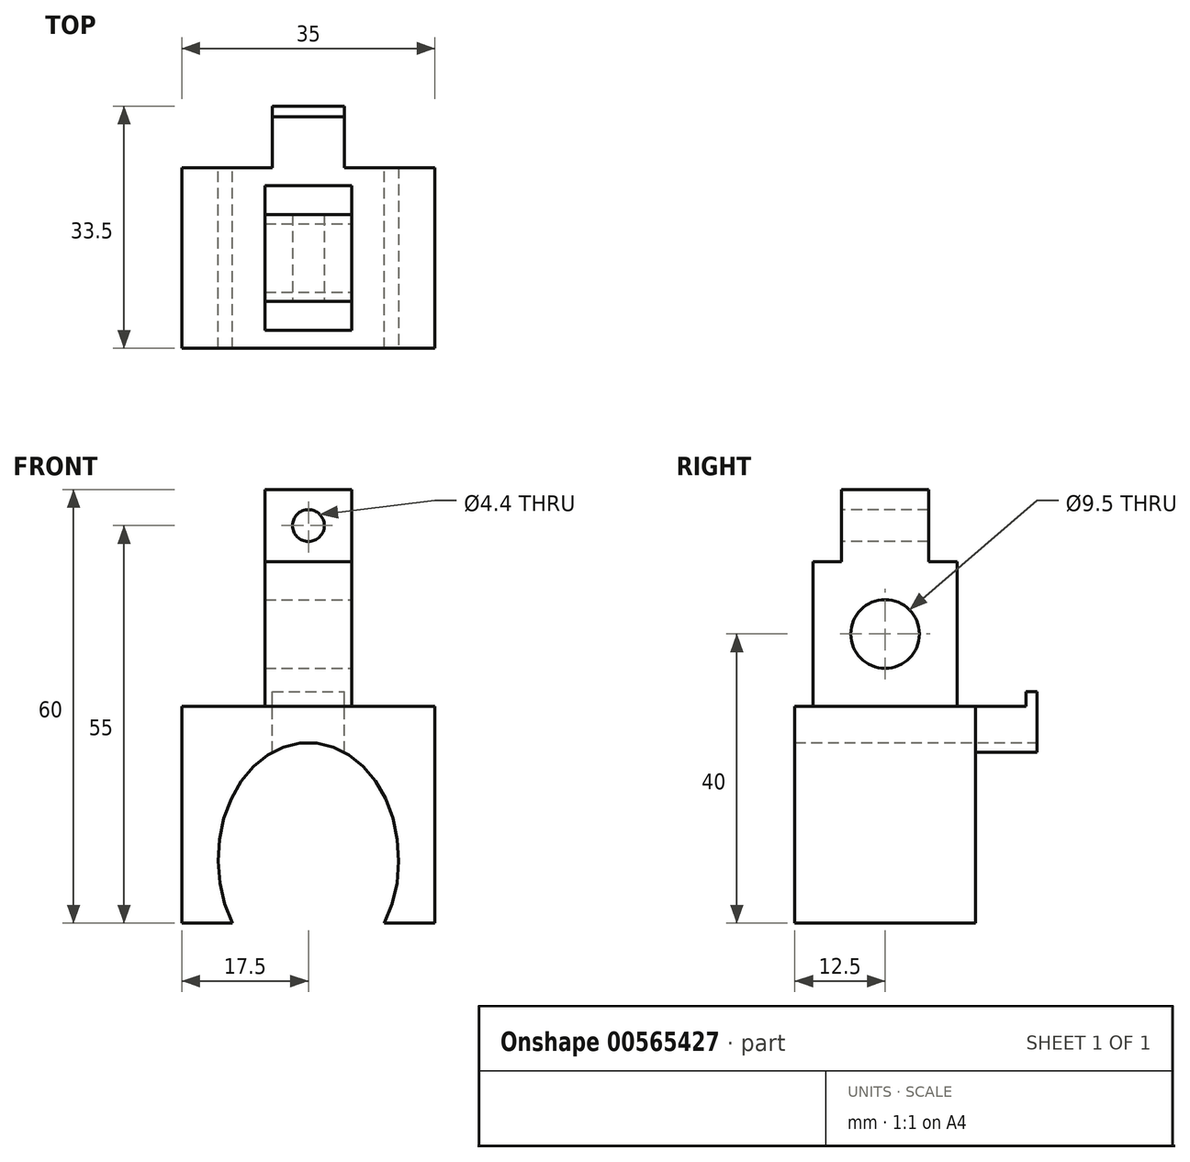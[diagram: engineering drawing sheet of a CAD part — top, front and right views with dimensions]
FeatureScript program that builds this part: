
annotation { "Feature Type Name" : "Feature", "Feature Type Description" : "" }
export const myFeature = defineFeature(function(context is Context, id is Id, definition is map)
    precondition{}
    {
        {
            var Q0;
            Q0=qCreatedBy(makeId("Front.planeOp"),FACE);
            var sketch = newSketch(context, id + "F0", { "sketchPlane" : qUnion([Q0])});
            skLineSegment(sketch, "E0.bottom", {"start": v(0, 0) * mm, "end": v(25, 0) * mm});
            skLineSegment(sketch, "E0.top", {"start": v(0, 32.5) * mm, "end": v(25, 32.5) * mm});
            skLineSegment(sketch, "E0.left", {"start": v(0, 0) * mm, "end": v(0, 32.5) * mm});
            skLineSegment(sketch, "E0.right", {"start": v(25, 0) * mm, "end": v(25, 32.5) * mm});
            skEllipse(sketch, "E1", {"center": v(12.5, 16.25) * mm, "majorRadius": 16.25 * mm, "minorRadius": 12.5 * mm, "majorAxis": v(0, -1)});
            skLineSegment(sketch, "E2.bottom", {"start": v(30, 37.5) * mm, "end": v(-5, 37.5) * mm});
            skLineSegment(sketch, "E2.top", {"start": v(30, 7.5) * mm, "end": v(-5, 7.5) * mm});
            skLineSegment(sketch, "E2.left", {"start": v(30, 37.5) * mm, "end": v(30, 7.5) * mm});
            skLineSegment(sketch, "E2.right", {"start": v(-5, 37.5) * mm, "end": v(-5, 7.5) * mm});
            skSolve(sketch);
        }
        {
            var Q0;
            Q0=makeQuery(id+"F0.imprint","IMPRINT",FACE,{"disambiguationData":[TD([[makeQuery(id+"F0.imprint","IMPRINT",EDGE,{"derivedFrom":sQuery(id+"F0.wireOp",EDGE,"E2.bottom")}),1.0]])]});
            var Q1;
            {var subQ0=sQuery(id+"F0.wireOp",EDGE,"E0.right");var subQ1=sQuery(id+"F0.wireOp",EDGE,"E0.top");var subQ2=makeQuery(id+"F0.imprint","INTERSECT",VERTEX,{"derivedFrom":[subQ1,subQ0]});Q1=makeQuery(id+"F0.imprint","IMPRINT",FACE,{"disambiguationData":[TD([[makeQuery(id+"F0.imprint","IMPRINT",EDGE,{"disambiguationData":[TD([[subQ2,1.0]])],"derivedFrom":subQ1}),-1.0]])]});}
            var Q2;
            {var subQ0=sQuery(id+"F0.wireOp",EDGE,"E0.left");var subQ1=sQuery(id+"F0.wireOp",EDGE,"E0.top");var subQ2=makeQuery(id+"F0.imprint","INTERSECT",VERTEX,{"derivedFrom":[subQ1,subQ0]});Q2=makeQuery(id+"F0.imprint","IMPRINT",FACE,{"disambiguationData":[TD([[makeQuery(id+"F0.imprint","IMPRINT",EDGE,{"disambiguationData":[TD([[subQ2,-1.0]])],"derivedFrom":subQ1}),-1.0]])]});}
            var Q3;
            {var subQ0=sQuery(id+"F0.wireOp",EDGE,"E2.top");var subQ1=sQuery(id+"F0.wireOp",EDGE,"E0.right");var subQ2=makeQuery(id+"F0.imprint","INTERSECT",VERTEX,{"derivedFrom":[subQ1,subQ0]});Q3=makeQuery(id+"F0.imprint","IMPRINT",FACE,{"disambiguationData":[TD([[makeQuery(id+"F0.imprint","IMPRINT",EDGE,{"disambiguationData":[TD([[subQ2,-1.0]])],"derivedFrom":subQ1}),1.0]])]});}
            var Q4;
            {var subQ0=sQuery(id+"F0.wireOp",EDGE,"E2.top");var subQ1=sQuery(id+"F0.wireOp",EDGE,"E0.left");var subQ2=makeQuery(id+"F0.imprint","INTERSECT",VERTEX,{"derivedFrom":[subQ1,subQ0]});Q4=makeQuery(id+"F0.imprint","IMPRINT",FACE,{"disambiguationData":[TD([[makeQuery(id+"F0.imprint","IMPRINT",EDGE,{"disambiguationData":[TD([[subQ2,-1.0]])],"derivedFrom":subQ1}),-1.0]])]});}
            extrude(context, id + "F1", {"entities" : qUnion([Q0, Q1, Q2, Q3, Q4]), "depth" : 25 * mm, "offsetDistance" : 25 * mm});
        }
        {
            var Q0;
            Q0=makeQuery(id+"F1.opExtrude","SWEPT_FACE",FACE,{"disambiguationData":[OSD([sQuery(id+"F0.wireOp",EDGE,"E2.left")])]});
            var Q1;
            Q1=makeQuery(id+"F1.opExtrude","SWEPT_FACE",FACE,{"disambiguationData":[OSD([sQuery(id+"F0.wireOp",EDGE,"E2.right")])]});
            cPlane(context, id + "F2", {"entities" : qUnion([Q0, Q1]), "cplaneType" : CPlaneType.MID_PLANE, "offset" : 25 * mm, "width" : 150 * mm, "height" : 150 * mm});
        }
        {
            var Q0;
            Q0=qCreatedBy(id+"F2.planeOp",FACE);
            var sketch = newSketch(context, id + "F3", { "sketchPlane" : qUnion([Q0])});
            skLineSegment(sketch, "E3.0", {"start": v(-25, 37.5) * mm, "end": v(0, 37.5) * mm});
            skLineSegment(sketch, "E4.bottom", {"start": v(-22.5, 57.5) * mm, "end": v(-2.5, 57.5) * mm});
            skLineSegment(sketch, "E4.top", {"start": v(-22.5, 37.5) * mm, "end": v(-2.5, 37.5) * mm});
            skLineSegment(sketch, "E4.left", {"start": v(-22.5, 57.5) * mm, "end": v(-22.5, 37.5) * mm});
            skLineSegment(sketch, "E4.right", {"start": v(-2.5, 57.5) * mm, "end": v(-2.5, 37.5) * mm});
            skLineSegment(sketch, "E5", {"start": v(-12.5, 37.5) * mm, "end": v(-12.5, 31.91) * mm, "construction": true});
            skSolve(sketch);
        }
        {
            var Q0;
            Q0=makeQuery(id+"F3.imprint","IMPRINT",FACE,{"disambiguationData":[TD([[makeQuery(id+"F3.imprint","IMPRINT",EDGE,{"derivedFrom":sQuery(id+"F3.wireOp",EDGE,"E4.bottom")}),-1.0]])]});
            extrude(context, id + "F4", {"entities" : qUnion([Q0]), "operationType" : NewBodyOperationType.ADD, "endBound" : BoundingType.SYMMETRIC, "depth" : 12 * mm, "offsetDistance" : 25 * mm});
        }
        {
            var Q0;
            Q0=makeQuery(id+"F4.opExtrude","CAP_FACE",FACE,{"disambiguationData":[OSD([sQuery(id+"F3.wireOp",EDGE,"E4.bottom"),sQuery(id+"F3.wireOp",EDGE,"E4.top"),sQuery(id+"F3.wireOp",EDGE,"E4.left"),sQuery(id+"F3.wireOp",EDGE,"E4.right")])],"isStart":false});
            var sketch = newSketch(context, id + "F5", { "sketchPlane" : qUnion([Q0])});
            skCircle(sketch, "E6", {"center": v(-12.5, 47.5) * mm, "radius": 4.75 * mm});
            skLineSegment(sketch, "E7", {"start": v(-22.5, 57.5) * mm, "end": v(-2.5, 37.5) * mm, "construction": true});
            skSolve(sketch);
        }
        {
            var Q0;
            Q0=makeQuery(id+"F5.imprint","IMPRINT",FACE,{"disambiguationData":[TD([[makeQuery(id+"F5.imprint","IMPRINT",EDGE,{"derivedFrom":sQuery(id+"F5.wireOp",EDGE,"E6")}),1.0]])]});
            extrude(context, id + "F6", {"entities" : qUnion([Q0]), "operationType" : NewBodyOperationType.REMOVE, "endBound" : BoundingType.THROUGH_ALL, "oppositeDirection" : true, "depth" : 25 * mm, "offsetDistance" : 25 * mm});
        }
        {
            var Q0;
            Q0=qCreatedBy(id+"F2.planeOp",FACE);
            var sketch = newSketch(context, id + "F7", { "sketchPlane" : qUnion([Q0])});
            skLineSegment(sketch, "E8.0", {"start": v(-22.5, 57.5) * mm, "end": v(-2.5, 57.5) * mm});
            skLineSegment(sketch, "E9.bottom", {"start": v(-18.5, 67.5) * mm, "end": v(-6.5, 67.5) * mm});
            skLineSegment(sketch, "E9.top", {"start": v(-18.5, 57.5) * mm, "end": v(-6.5, 57.5) * mm});
            skLineSegment(sketch, "E9.left", {"start": v(-18.5, 67.5) * mm, "end": v(-18.5, 57.5) * mm});
            skLineSegment(sketch, "E9.right", {"start": v(-6.5, 67.5) * mm, "end": v(-6.5, 57.5) * mm});
            skPoint(sketch, "E10", {"position": v(-12.5, 57.5) * mm});
            skSolve(sketch);
        }
        {
            var Q0;
            Q0=makeQuery(id+"F7.imprint","IMPRINT",FACE,{"disambiguationData":[TD([[makeQuery(id+"F7.imprint","IMPRINT",EDGE,{"derivedFrom":sQuery(id+"F7.wireOp",EDGE,"E9.bottom")}),-1.0]])]});
            extrude(context, id + "F8", {"entities" : qUnion([Q0]), "operationType" : NewBodyOperationType.ADD, "endBound" : BoundingType.SYMMETRIC, "depth" : 12 * mm, "offsetDistance" : 25 * mm});
        }
        {
            var Q0;
            Q0=makeQuery(id+"F8.boolean.opBoolean","MERGE",FACE,{"derivedFrom":[makeQuery(id+"F4.opExtrude","CAP_FACE",FACE,{"disambiguationData":[OSD([sQuery(id+"F3.wireOp",EDGE,"E4.bottom"),sQuery(id+"F3.wireOp",EDGE,"E4.top"),sQuery(id+"F3.wireOp",EDGE,"E4.left"),sQuery(id+"F3.wireOp",EDGE,"E4.right")])],"isStart":false}),makeQuery(id+"F8.opExtrude","CAP_FACE",FACE,{"disambiguationData":[OSD([sQuery(id+"F7.wireOp",EDGE,"E9.bottom"),sQuery(id+"F7.wireOp",EDGE,"E9.top"),sQuery(id+"F7.wireOp",EDGE,"E9.left"),sQuery(id+"F7.wireOp",EDGE,"E9.right")])],"isStart":false})]});
            var sketch = newSketch(context, id + "F9", { "sketchPlane" : qUnion([Q0])});
            skPoint(sketch, "E11.0", {"position": v(-12.5, 67.5) * mm});
            skLineSegment(sketch, "E12.0", {"start": v(-18.5, 67.5) * mm, "end": v(-6.5, 67.5) * mm});
            skCircle(sketch, "E13.0", {"center": v(-12.5, 47.5) * mm, "radius": 4.75 * mm});
            skLineSegment(sketch, "E14.bottom", {"start": v(-13.15, 47.5) * mm, "end": v(-11.85, 47.5) * mm});
            skLineSegment(sketch, "E14.top", {"start": v(-13.15, 67.5) * mm, "end": v(-11.85, 67.5) * mm});
            skLineSegment(sketch, "E14.left", {"start": v(-13.15, 47.5) * mm, "end": v(-13.15, 67.5) * mm});
            skLineSegment(sketch, "E14.right", {"start": v(-11.85, 47.5) * mm, "end": v(-11.85, 67.5) * mm});
            skSolve(sketch);
        }
        {
            var Q0;
            {var subQ5=sQuery(id+"F9.wireOp",EDGE,"E14.top");Q0=makeQuery(id+"F9.imprint","IMPRINT",FACE,{"disambiguationData":[TD([[makeQuery(id+"F9.imprint","IMPRINT",EDGE,{"derivedFrom":subQ5}),-1.0]])]});}
            var Q1;
            {var subQ5=sQuery(id+"F9.wireOp",EDGE,"E14.bottom");Q1=makeQuery(id+"F9.imprint","IMPRINT",FACE,{"disambiguationData":[TD([[makeQuery(id+"F9.imprint","IMPRINT",EDGE,{"derivedFrom":subQ5}),1.0]])]});}
            extrude(context, id + "F10", {"entities" : qUnion([Q0, Q1]), "operationType" : NewBodyOperationType.REMOVE, "endBound" : BoundingType.THROUGH_ALL, "oppositeDirection" : true, "depth" : 25 * mm, "offsetDistance" : 25 * mm});
        }
        {
            var Q0;
            Q0=makeQuery(id+"F8.opExtrude","SWEPT_FACE",FACE,{"disambiguationData":[OSD([sQuery(id+"F7.wireOp",EDGE,"E9.left")])]});
            var sketch = newSketch(context, id + "F11", { "sketchPlane" : qUnion([Q0])});
            skLineSegment(sketch, "E15", {"start": v(6.5, 67.5) * mm, "end": v(18.5, 57.5) * mm, "construction": true});
            skCircle(sketch, "E16", {"center": v(12.5, 62.5) * mm, "radius": 2.2 * mm});
            skSolve(sketch);
        }
        {
            var Q0;
            Q0=makeQuery(id+"F11.imprint","IMPRINT",FACE,{"disambiguationData":[TD([[makeQuery(id+"F11.imprint","IMPRINT",EDGE,{"derivedFrom":sQuery(id+"F11.wireOp",EDGE,"E16")}),1.0]])]});
            extrude(context, id + "F12", {"entities" : qUnion([Q0]), "operationType" : NewBodyOperationType.REMOVE, "endBound" : BoundingType.THROUGH_ALL, "oppositeDirection" : true, "depth" : 25 * mm, "offsetDistance" : 25 * mm});
        }
        {
            var Q0;
            Q0=makeQuery(id+"F1.opExtrude","CAP_FACE",FACE,{"disambiguationData":[OSD([sQuery(id+"F0.wireOp",EDGE,"E1"),sQuery(id+"F0.wireOp",EDGE,"E2.bottom"),sQuery(id+"F0.wireOp",EDGE,"E2.top"),sQuery(id+"F0.wireOp",EDGE,"E2.left"),sQuery(id+"F0.wireOp",EDGE,"E2.right")])],"isStart":true});
            var sketch = newSketch(context, id + "F13", { "sketchPlane" : qUnion([Q0])});
            skEllipticalArc(sketch, "E17.0", {});
            skLineSegment(sketch, "E18.bottom", {"start": v(-7.5, 16.25) * mm, "end": v(-17.5, 16.25) * mm});
            skLineSegment(sketch, "E18.top", {"start": v(-7.5, 37.5) * mm, "end": v(-17.5, 37.5) * mm});
            skLineSegment(sketch, "E18.left", {"start": v(-7.5, 16.25) * mm, "end": v(-7.5, 37.5) * mm});
            skLineSegment(sketch, "E18.right", {"start": v(-17.5, 16.25) * mm, "end": v(-17.5, 37.5) * mm});
            const initialGuessF13  = {"E17.0": [-0.0125, 0.01625, 0, -1, 0.01625, 0.0125, 1.0021860265307148, 5.280999280648871]};
            skSetInitialGuess(sketch, initialGuessF13);
            skSolve(sketch);
        }
        {
            var Q0;
            {var subQ5=sQuery(id+"F13.wireOp",EDGE,"E18.top");Q0=makeQuery(id+"F13.imprint","IMPRINT",FACE,{"disambiguationData":[TD([[makeQuery(id+"F13.imprint","IMPRINT",EDGE,{"derivedFrom":subQ5}),-1.0]])]});}
            extrude(context, id + "F14", {"entities" : qUnion([Q0]), "operationType" : NewBodyOperationType.ADD, "depth" : 7 * mm, "offsetDistance" : 25 * mm});
        }
        {
            var Q0;
            Q0=makeQuery(id+"F14.opExtrude","CAP_FACE",FACE,{"disambiguationData":[OSD([sQuery(id+"F13.wireOp",EDGE,"E17.0"),sQuery(id+"F13.wireOp",EDGE,"E18.top"),sQuery(id+"F13.wireOp",EDGE,"E18.left"),sQuery(id+"F13.wireOp",EDGE,"E18.right")])],"isStart":false});
            var sketch = newSketch(context, id + "F15", { "sketchPlane" : qUnion([Q0])});
            skLineSegment(sketch, "E19.0.0", {"start": v(-17.5, 37.5) * mm, "end": v(-17.5, 31.14) * mm});
            skEllipticalArc(sketch, "E19.0.1", {});
            skLineSegment(sketch, "E19.0.2", {"start": v(-7.5, 31.14) * mm, "end": v(-7.5, 37.5) * mm});
            skLineSegment(sketch, "E19.0.3", {"start": v(-7.5, 37.5) * mm, "end": v(-17.5, 37.5) * mm});
            skLineSegment(sketch, "E20.top", {"start": v(-7.5, 39.5) * mm, "end": v(-17.5, 39.5) * mm});
            skLineSegment(sketch, "E20.left", {"start": v(-7.5, 37.5) * mm, "end": v(-7.5, 39.5) * mm});
            skLineSegment(sketch, "E20.right", {"start": v(-17.5, 37.5) * mm, "end": v(-17.5, 39.5) * mm});
            const initialGuessF15  = {"E19.0.1": [-0.0125, 0.01625, 0, -1, 0.01625, 0.0125, 2.730075807522306, 3.5531094996572814]};
            skSetInitialGuess(sketch, initialGuessF15);
            skSolve(sketch);
        }
        {
            var Q0;
            Q0=makeQuery(id+"F15.imprint","IMPRINT",FACE,{"disambiguationData":[TD([[makeQuery(id+"F15.imprint","IMPRINT",EDGE,{"derivedFrom":sQuery(id+"F15.wireOp",EDGE,"E19.0.3")}),1.0]])]});
            var Q1;
            Q1=makeQuery(id+"F15.imprint","IMPRINT",FACE,{"disambiguationData":[TD([[makeQuery(id+"F15.imprint","IMPRINT",EDGE,{"derivedFrom":sQuery(id+"F15.wireOp",EDGE,"E19.0.0")}),-1.0]])]});
            extrude(context, id + "F16", {"entities" : qUnion([Q0, Q1]), "operationType" : NewBodyOperationType.ADD, "depth" : 1.5 * mm, "offsetDistance" : 25 * mm});
        }
        {
            var Q0;
            {var subQ0=sQuery(id+"F0.wireOp",EDGE,"E2.left");var subQ1=sQuery(id+"F0.wireOp",EDGE,"E2.top");var subQ3=sQuery(id+"F0.wireOp",EDGE,"E1");var subQ4=sQuery(id+"F0.wireOp",EDGE,"E2.bottom");Q0=makeQuery(id+"F14.boolean.opBoolean","SPLIT",FACE,{"disambiguationData":[TD([makeQuery(id+"F1.opExtrude","SWEPT_FACE",FACE,{"disambiguationData":[OSD([subQ0])]})])],"derivedFrom":makeQuery(id+"F1.opExtrude","CAP_FACE",FACE,{"disambiguationData":[OSD([subQ3,subQ4,subQ1,subQ0,sQuery(id+"F0.wireOp",EDGE,"E2.right")])],"isStart":true})});}
            var Q1;
            Q1=makeQuery(id+"F1.opExtrude","CAP_FACE",FACE,{"disambiguationData":[OSD([sQuery(id+"F0.wireOp",EDGE,"E1"),sQuery(id+"F0.wireOp",EDGE,"E2.bottom"),sQuery(id+"F0.wireOp",EDGE,"E2.top"),sQuery(id+"F0.wireOp",EDGE,"E2.left"),sQuery(id+"F0.wireOp",EDGE,"E2.right")])],"isStart":false});
            cPlane(context, id + "F17", {"entities" : qUnion([Q0, Q1]), "cplaneType" : CPlaneType.MID_PLANE, "offset" : 25 * mm, "width" : 150 * mm, "height" : 150 * mm});
        }
    });
